# Revit family: Window_Shade-Draper_Inc.-Motorized_Flex
name_source: partatom
category: Specialty Equipment
revit_build: Autodesk Revit Architecture 2012 (Build: 20110309_2315(x64)
units: mm (PartAtom-declared; Revit-internal decimal feet)

## types (8) — shared parameters
24V DC Quiet Motor = No
Battery Operated Motor = No
D1 = 5/8"
Description = Motorized Shade
Fascia Material = Paint - Draper - White
Frequency = 60 Hz
Manufacturer = Draper Inc.
Min Length = 2' - 0"
Model = Motorized Flex
Notes = Maximum size 168” x 168”. Other sizes available. Contact Draper for details.
Number of Poles = 1
Phase = 1
Power Factor = 1
Product Documentation Link = http://www.draperinc.com
Product Name = Motorized FlexShade
Product Page URL = http://www.draperinc.com
Quiet Motor = No
R.T.S. Motor = No
Shade Material = Fabric - Draper - Green Screen Revive 5%
Standard 120V Motor = Yes
URL = http://www.DraperInc.com
Voltage = 120 V

## per-type parameters (varying)
| type | A1 | A2 | Apparent Load | B1 | B2 | Brackets Only | C1 | C2 | Constraint Length | Depth | E1 | Head Box | Length | Not BO | Overall Height | Radius Fascia | Square Fascia | Width |
| Large - Square Fascia | 4 11/16" | 2 1/2" | 0 VA | 4 11/16" | 1 5/8" | No | 1 9/16" | 3/4" | 8' - 2 7/8" | 4 11/16" | 3/32" | No | 8' - 2 7/8" | Yes | 5' - 9 1/2" | No | Yes | 4 11/16" |
| Small - Square Fascia | 3 15/16" | 0" | 156 VA | 3 7/16" | 0" | No | 1 3/16" | 0" | 4' - 0" | 3 15/16" | 1/16" | No | 4' - 0" | Yes | 6' - 0" | No | Yes | 3 7/16" |
| Large - Radius Fascia | 4 11/16" | 2 1/2" | 0 VA | 4 11/16" | 1 5/8" | No | 1 9/16" | 3/4" | 8' - 2 7/8" | 4 11/16" | 3/32" | No | 8' - 2 7/8" | Yes | 5' - 9 1/2" | Yes | No | 4 11/16" |
| Small - Radius Fascia | 3 15/16" | 0" | 156 VA | 3 7/16" | 0" | No | 1 3/16" | 0" | 4' - 0" | 3 15/16" | 1/16" | No | 4' - 0" | Yes | 6' - 0" | Yes | No | 3 7/16" |
| Large - Headbox | 4 11/16" | 2 1/2" | 0 VA | 4 11/16" | 1 5/8" | No | 1 9/16" | 3/4" | 8' - 2 7/8" | 4 11/16" | 3/32" | Yes | 8' - 2 7/8" | Yes | 5' - 9 1/2" | No | No | 4 11/16" |
| Small - Headbox | 3 15/16" | 0" | 156 VA | 3 7/16" | 0" | No | 1 3/16" | 0" | 4' - 0" | 3 15/16" | 1/16" | Yes | 4' - 0" | Yes | 6' - 0" | No | No | 3 7/16" |
| Large - Bracket Only | 4 11/16" | 2 1/2" | 0 VA | 4 11/16" | 1 5/8" | Yes | 1 9/16" | 3/4" | 8' - 2 7/8" | 4 11/16" | 3/32" | No | 8' - 2 7/8" | No | 5' - 9 1/2" | No | No | 4 11/16" |
| Small - Bracket Only | 3 15/16" | 0" | 156 VA | 3 7/16" | 0" | Yes | 1 3/16" | 0" | 4' - 0" | 3 15/16" | 1/16" | No | 4' - 0" | No | 6' - 0" | No | No | 3 7/16" |

## geometry (parser evidence)
native form markers: Blend x2, Sweep x10
no freeform markers — native parametric forms only
